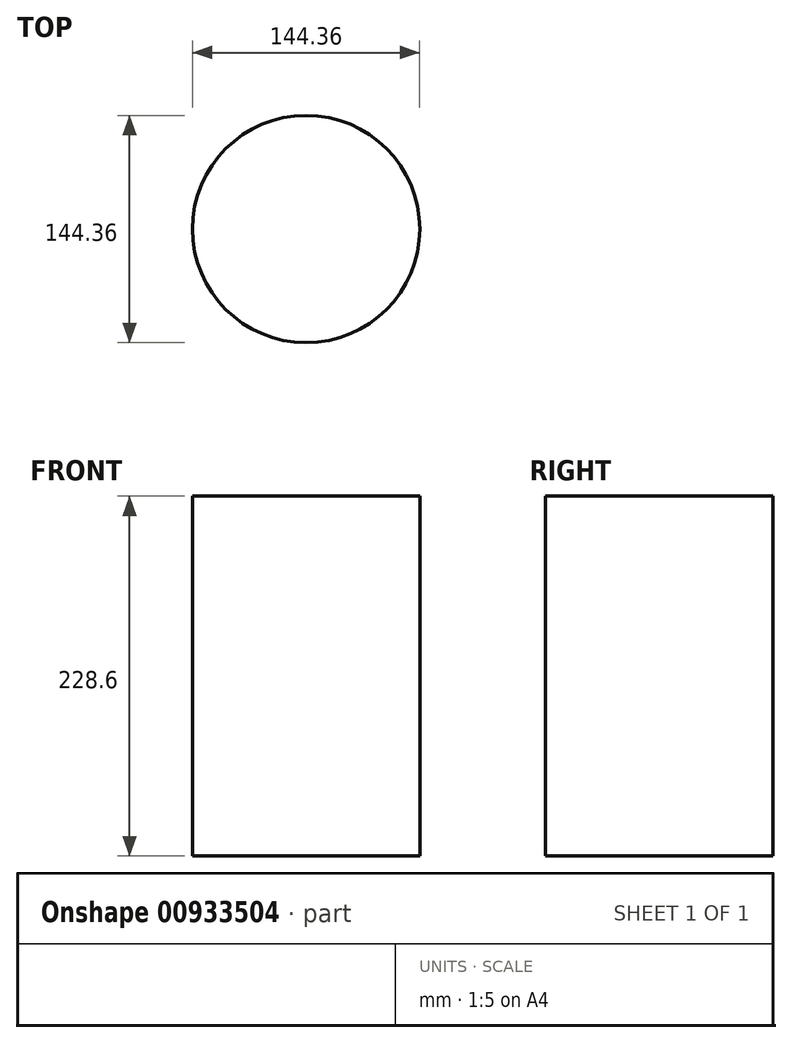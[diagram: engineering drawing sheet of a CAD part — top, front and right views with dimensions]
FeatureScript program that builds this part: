
annotation { "Feature Type Name" : "Feature", "Feature Type Description" : "" }
export const myFeature = defineFeature(function(context is Context, id is Id, definition is map)
    precondition{}
    {
        {
            var Q0;
            Q0=qCreatedBy(makeId("Top.planeOp"),FACE);
            var sketch = newSketch(context, id + "F0", { "sketchPlane" : qUnion([Q0])});
            skCircle(sketch, "E0", {"center": v(0, 0) * mm, "radius": 72.18 * mm});
            skLineSegment(sketch, "E1", {"start": v(59.36, -41.08) * mm, "end": v(115.63, -139.94) * mm});
            skSolve(sketch);
        }
        {
            var Q0;
            Q0 = qSketchRegion(id + "F0", true);
            extrude(context, id + "F1", {"entities" : qUnion([Q0]), "depth" : 25.4 * mm, "offsetDistance" : 25.4 * mm});
        }
        {
            var Q0;
            Q0=makeQuery(id+"F1.opExtrude","CAP_FACE",FACE,{"disambiguationData":[OSD([sQuery(id+"F0.wireOp",EDGE,"E0")])],"isStart":false});
            extrude(context, id + "F2", {"entities" : qUnion([Q0]), "operationType" : NewBodyOperationType.ADD, "depth" : 203.2 * mm, "offsetDistance" : 25.4 * mm});
        }
    });
